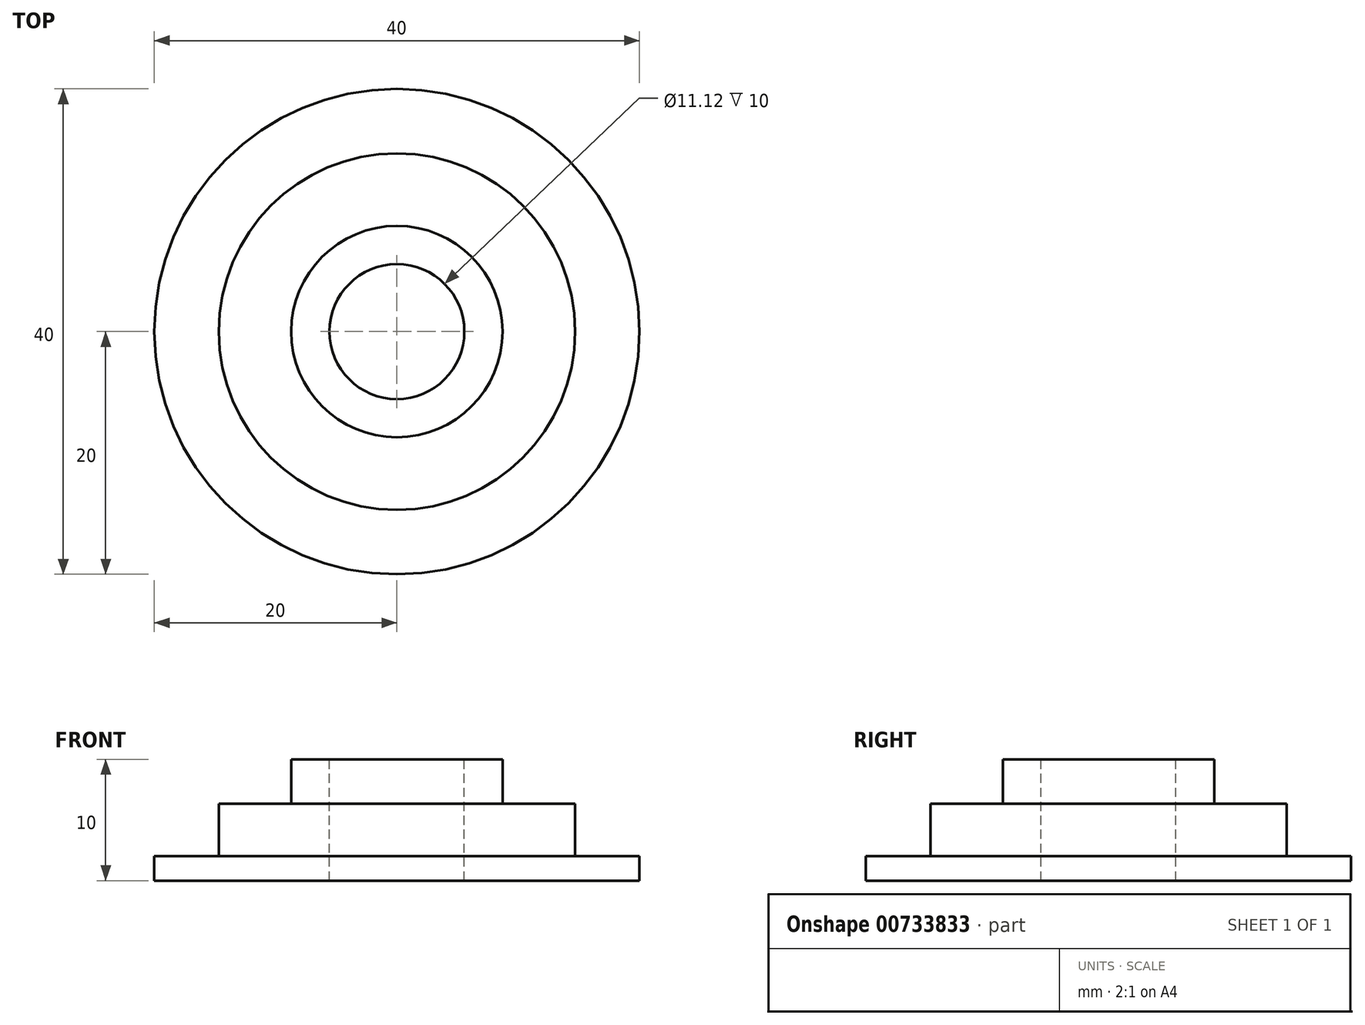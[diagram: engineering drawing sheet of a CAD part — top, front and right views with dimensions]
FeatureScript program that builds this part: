
annotation { "Feature Type Name" : "Feature", "Feature Type Description" : "" }
export const myFeature = defineFeature(function(context is Context, id is Id, definition is map)
    precondition{}
    {
        {
            var Q0;
            Q0=qCreatedBy(makeId("Front.planeOp"),FACE);
            var sketch = newSketch(context, id + "F0", { "sketchPlane" : qUnion([Q0])});
            skLineSegment(sketch, "E0", {"start": v(5.56, 0) * mm, "end": v(20, 0) * mm});
            skLineSegment(sketch, "E1", {"start": v(20, 0) * mm, "end": v(20, 2.03) * mm});
            skLineSegment(sketch, "E2", {"start": v(20, 2.03) * mm, "end": v(14.69, 2.03) * mm});
            skLineSegment(sketch, "E3", {"start": v(14.69, 2.03) * mm, "end": v(14.69, 6.35) * mm});
            skLineSegment(sketch, "E4", {"start": v(14.69, 6.35) * mm, "end": v(8.71, 6.35) * mm});
            skLineSegment(sketch, "E5", {"start": v(8.71, 6.35) * mm, "end": v(8.71, 10) * mm});
            skLineSegment(sketch, "E6", {"start": v(8.71, 10) * mm, "end": v(5.56, 10) * mm});
            skLineSegment(sketch, "E7", {"start": v(5.56, 10) * mm, "end": v(5.56, 0) * mm});
            skSolve(sketch);
        }
        {
            var Q0;
            Q0=qCreatedBy(makeId("Front.planeOp"),FACE);
            var sketch = newSketch(context, id + "F1", { "sketchPlane" : qUnion([Q0])});
            skLineSegment(sketch, "E8", {"start": v(0, 29.28) * mm, "end": v(0, -19.17) * mm, "construction": true});
            skSolve(sketch);
        }
        {
            var Q0;
            Q0=makeQuery(id+"F0.imprint","IMPRINT",FACE,{"disambiguationData":[TD([[makeQuery(id+"F0.imprint","IMPRINT",EDGE,{"derivedFrom":sQuery(id+"F0.wireOp",EDGE,"E0")}),1.0]])]});
            var Q1;
            Q1=sQuery(id+"F1.wireOp",EDGE,"E8");
            revolve(context, id + "F2", {"surfaceOperationType" : NewSurfaceOperationType.NEW, "entities" : qUnion([Q0]), "axis" : qUnion([Q1]), "revolveType" : RevolveType.FULL});
        }
    });
